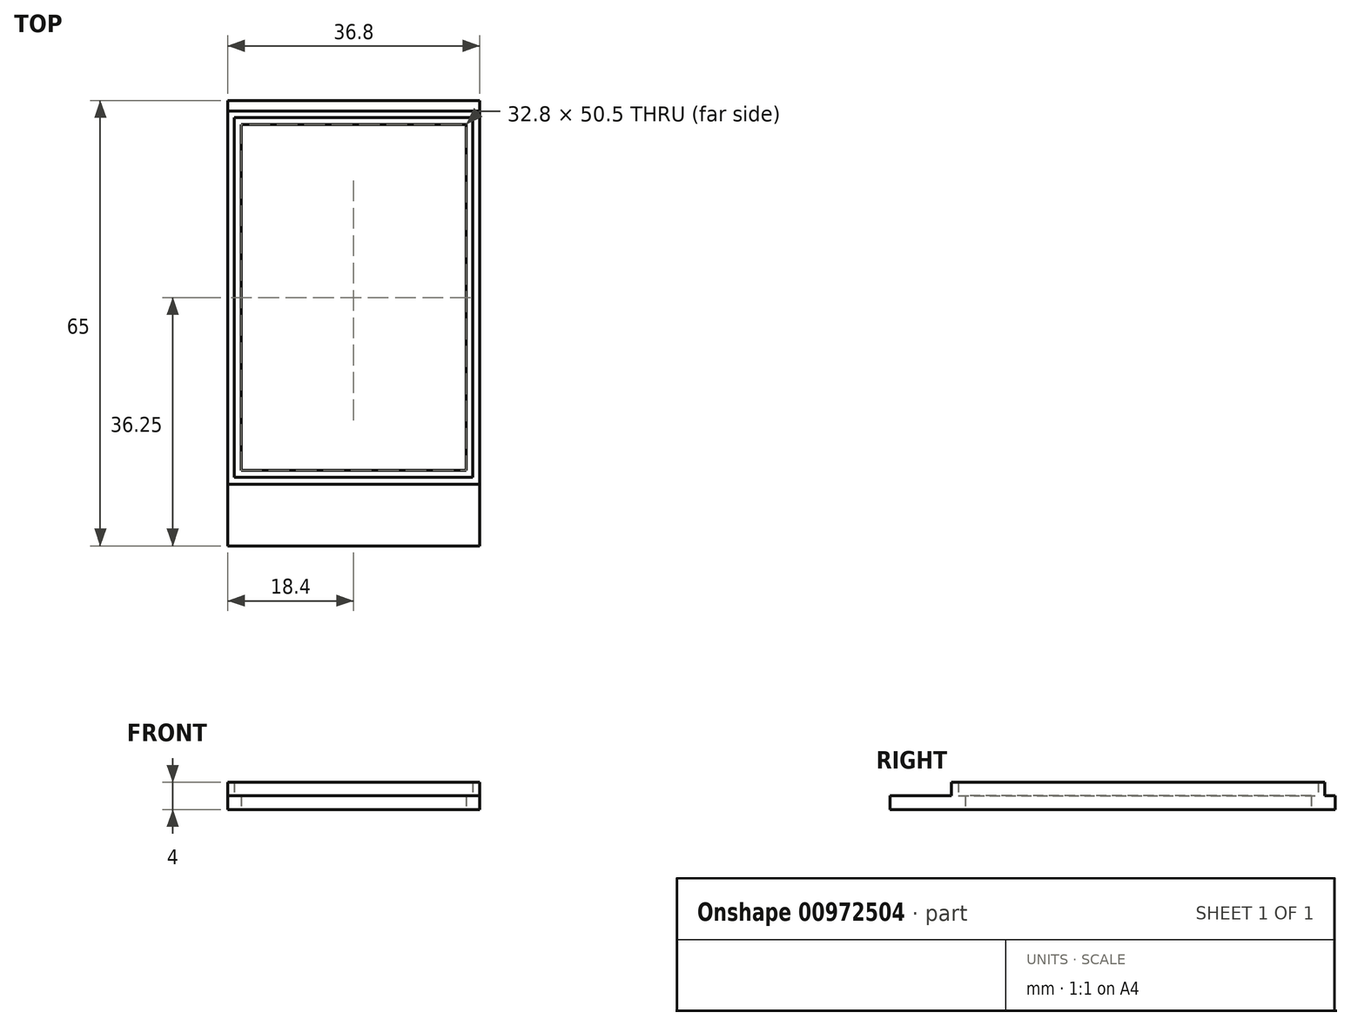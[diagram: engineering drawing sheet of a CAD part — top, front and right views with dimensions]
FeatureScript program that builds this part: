
annotation { "Feature Type Name" : "Feature", "Feature Type Description" : "" }
export const myFeature = defineFeature(function(context is Context, id is Id, definition is map)
    precondition{}
    {
        {
            var Q0;
            Q0=qCreatedBy(makeId("Top.planeOp"),FACE);
            var sketch = newSketch(context, id + "F0", { "sketchPlane" : qUnion([Q0])});
            skLineSegment(sketch, "E0.bottom", {"start": v(-17.4, 26.25) * mm, "end": v(17.4, 26.25) * mm});
            skLineSegment(sketch, "E0.top", {"start": v(-17.4, -26.25) * mm, "end": v(17.4, -26.25) * mm});
            skLineSegment(sketch, "E0.left", {"start": v(-17.4, 26.25) * mm, "end": v(-17.4, -26.25) * mm});
            skLineSegment(sketch, "E0.right", {"start": v(17.4, 26.25) * mm, "end": v(17.4, -26.25) * mm});
            skPoint(sketch, "E0.middle", {"position": v(0, 0) * mm});
            skLineSegment(sketch, "E1.0", {"start": v(-18.4, 27.25) * mm, "end": v(-18.4, -27.25) * mm});
            skLineSegment(sketch, "E1.1", {"start": v(-18.4, 27.25) * mm, "end": v(18.4, 27.25) * mm});
            skLineSegment(sketch, "E1.2", {"start": v(18.4, 27.25) * mm, "end": v(18.4, -27.25) * mm});
            skLineSegment(sketch, "E1.3", {"start": v(-18.4, -27.25) * mm, "end": v(18.4, -27.25) * mm});
            skLineSegment(sketch, "E2.0", {"start": v(-16.4, 25.25) * mm, "end": v(16.4, 25.25) * mm});
            skLineSegment(sketch, "E2.1", {"start": v(-16.4, 25.25) * mm, "end": v(-16.4, -25.25) * mm});
            skLineSegment(sketch, "E2.2", {"start": v(-16.4, -25.25) * mm, "end": v(16.4, -25.25) * mm});
            skLineSegment(sketch, "E2.3", {"start": v(16.4, 25.25) * mm, "end": v(16.4, -25.25) * mm});
            skLineSegment(sketch, "E3.bottom", {"start": v(-18.4, 28.75) * mm, "end": v(18.4, 28.75) * mm});
            skLineSegment(sketch, "E3.top", {"start": v(-18.4, -36.25) * mm, "end": v(18.4, -36.25) * mm});
            skLineSegment(sketch, "E3.left", {"start": v(-18.4, 28.75) * mm, "end": v(-18.4, -36.25) * mm});
            skLineSegment(sketch, "E3.right", {"start": v(18.4, 28.75) * mm, "end": v(18.4, -36.25) * mm});
            skSolve(sketch);
        }
        {
            var Q0;
            Q0 = qSketchRegion(id + "F0", true);
            var Q1;
            Q1=makeQuery(id+"F0.imprint","IMPRINT",FACE,{"disambiguationData":[TD([[makeQuery(id+"F0.imprint","IMPRINT",EDGE,{"derivedFrom":sQuery(id+"F0.wireOp",EDGE,"E0.bottom")}),-1.0]])]});
            extrude(context, id + "F1", {"entities" : qUnion([Q0, Q1]), "depth" : 2 * mm, "offsetDistance" : 25 * mm});
        }
        {
            var Q0;
            Q0=makeQuery(id+"F0.imprint","IMPRINT",FACE,{"disambiguationData":[TD([[makeQuery(id+"F0.imprint","IMPRINT",EDGE,{"derivedFrom":sQuery(id+"F0.wireOp",EDGE,"E0.bottom")}),1.0]])]});
            extrude(context, id + "F2", {"entities" : qUnion([Q0]), "operationType" : NewBodyOperationType.ADD, "depth" : 4 * mm, "offsetDistance" : 25 * mm});
        }
    });
